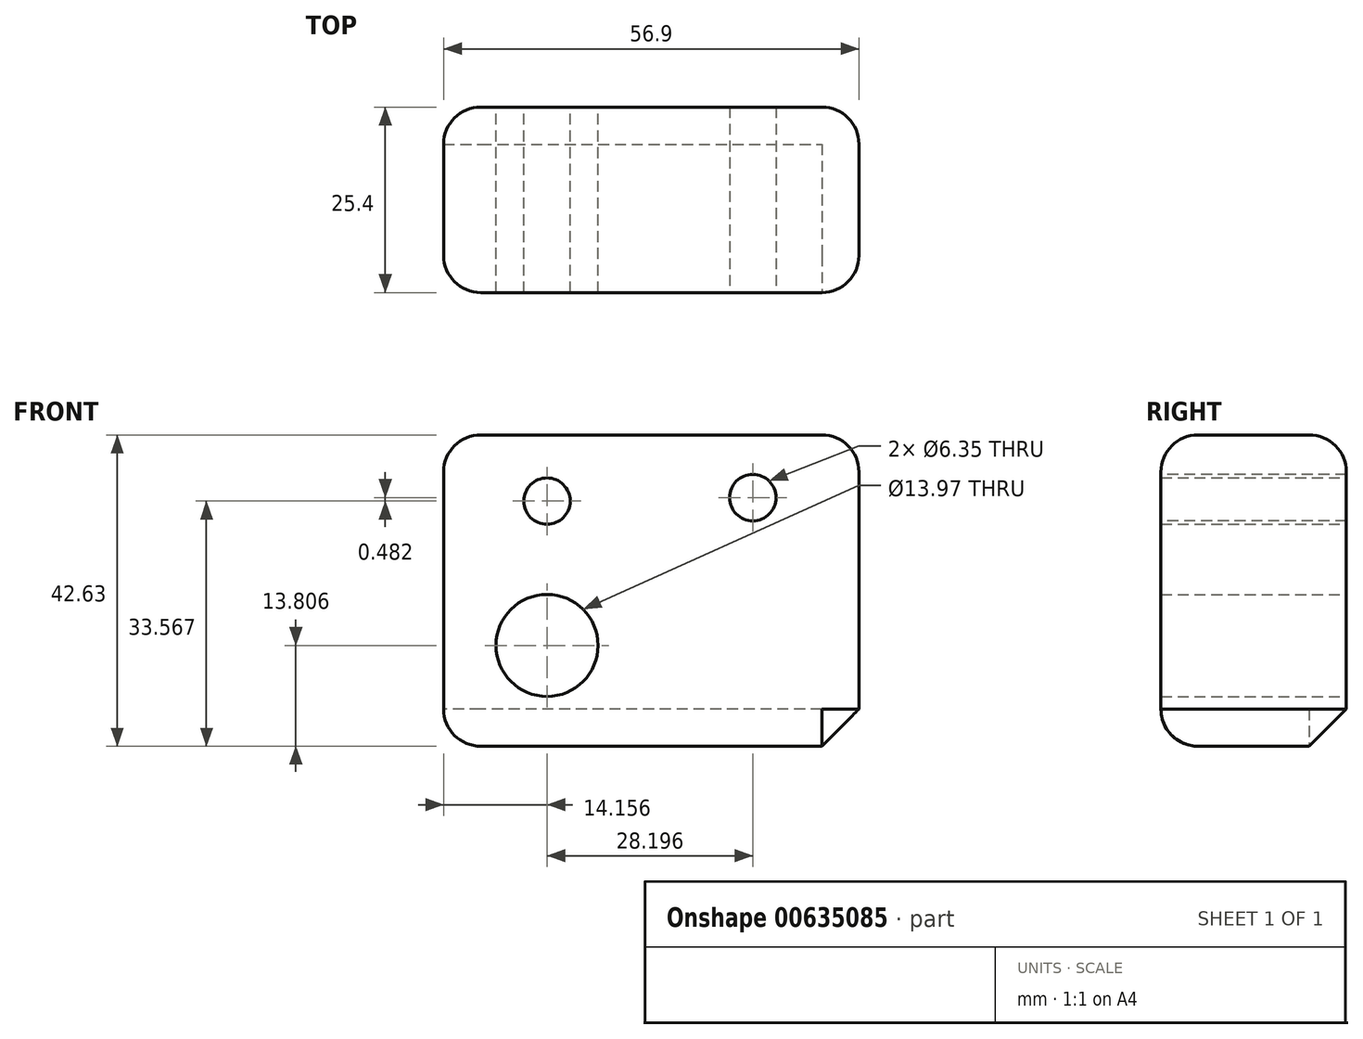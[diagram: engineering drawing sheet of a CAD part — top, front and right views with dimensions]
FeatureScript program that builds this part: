
annotation { "Feature Type Name" : "Feature", "Feature Type Description" : "" }
export const myFeature = defineFeature(function(context is Context, id is Id, definition is map)
    precondition{}
    {
        {
            var Q0;
            Q0=qCreatedBy(makeId("Front.planeOp"),FACE);
            var sketch = newSketch(context, id + "F0", { "sketchPlane" : qUnion([Q0])});
            skLineSegment(sketch, "E0.bottom", {"start": v(-32.11, 18.1) * mm, "end": v(24.79, 18.1) * mm});
            skLineSegment(sketch, "E0.top", {"start": v(-32.11, -24.53) * mm, "end": v(24.79, -24.53) * mm});
            skLineSegment(sketch, "E0.left", {"start": v(-32.11, 18.1) * mm, "end": v(-32.11, -24.53) * mm});
            skLineSegment(sketch, "E0.right", {"start": v(24.79, 18.1) * mm, "end": v(24.79, -24.53) * mm});
            skSolve(sketch);
        }
        {
            var Q0;
            Q0=makeQuery(id+"F0.imprint","IMPRINT",FACE,{"disambiguationData":[TD([[makeQuery(id+"F0.imprint","IMPRINT",EDGE,{"derivedFrom":sQuery(id+"F0.wireOp",EDGE,"E0.bottom")}),-1.0]])]});
            extrude(context, id + "F1", {"entities" : qUnion([Q0]), "oppositeDirection" : true, "depth" : 25.4 * mm, "offsetDistance" : 25.4 * mm});
        }
        {
            var Q0;
            Q0=qCreatedBy(makeId("Front.planeOp"),FACE);
            var sketch = newSketch(context, id + "F2", { "sketchPlane" : qUnion([Q0])});
            skCircle(sketch, "E1", {"center": v(10.24, 9.52) * mm, "radius": 5.03 * mm});
            skCircle(sketch, "E2", {"center": v(-5.18, 9.28) * mm, "radius": 2.06 * mm});
            skSolve(sketch);
        }
        {
            var Q0;
            Q0=sQuery(id+"F2.wireOp",VERTEX,"E1.center");
            var Q1;
            Q1=makeQuery(id+"F1.opExtrude","SWEPT_BODY",BODY,{"disambiguationData":[OSD([sQuery(id+"F0.wireOp",EDGE,"E0.bottom"),sQuery(id+"F0.wireOp",EDGE,"E0.top"),sQuery(id+"F0.wireOp",EDGE,"E0.left"),sQuery(id+"F0.wireOp",EDGE,"E0.right")])]});
            hole(context, id + "F3", {"style" : HoleStyle.SIMPLE, "endStyle" : HoleEndStyle.THROUGH, "holeDiameter" : 6.35 * mm, "majorDiameter" : 6.35 * mm, "isTappedThrough" : true, "tappedDepth" : 12.7 * mm, "tapClearance" : 3, "locations" : qUnion([Q0]), "scope" : qUnion([Q1])});
        }
        {
            var Q0;
            Q0=makeQuery(id+"F1.opExtrude","CAP_FACE",FACE,{"disambiguationData":[OSD([sQuery(id+"F0.wireOp",EDGE,"E0.bottom"),sQuery(id+"F0.wireOp",EDGE,"E0.top"),sQuery(id+"F0.wireOp",EDGE,"E0.left"),sQuery(id+"F0.wireOp",EDGE,"E0.right")])],"isStart":false});
            var sketch = newSketch(context, id + "F4", { "sketchPlane" : qUnion([Q0])});
            skCircle(sketch, "E3", {"center": v(17.95, 9.04) * mm, "radius": 3.58 * mm});
            skSolve(sketch);
        }
        {
            var Q0;
            Q0=sQuery(id+"F4.wireOp",VERTEX,"E3.center");
            var Q1;
            Q1=makeQuery(id+"F1.opExtrude","SWEPT_BODY",BODY,{"disambiguationData":[OSD([sQuery(id+"F0.wireOp",EDGE,"E0.bottom"),sQuery(id+"F0.wireOp",EDGE,"E0.top"),sQuery(id+"F0.wireOp",EDGE,"E0.left"),sQuery(id+"F0.wireOp",EDGE,"E0.right")])]});
            hole(context, id + "F5", {"style" : HoleStyle.SIMPLE, "endStyle" : HoleEndStyle.THROUGH, "holeDiameter" : 6.35 * mm, "majorDiameter" : 6.35 * mm, "isTappedThrough" : true, "tappedDepth" : 12.7 * mm, "tapClearance" : 3, "locations" : qUnion([Q0]), "scope" : qUnion([Q1])});
        }
        {
            var Q0;
            Q0=makeQuery(id+"F1.opExtrude","CAP_FACE",FACE,{"disambiguationData":[OSD([sQuery(id+"F0.wireOp",EDGE,"E0.bottom"),sQuery(id+"F0.wireOp",EDGE,"E0.top"),sQuery(id+"F0.wireOp",EDGE,"E0.left"),sQuery(id+"F0.wireOp",EDGE,"E0.right")])],"isStart":false});
            var sketch = newSketch(context, id + "F6", { "sketchPlane" : qUnion([Q0])});
            skSolve(sketch);
        }
        {
            var Q0;
            {var subQ3=sQuery(id+"F0.wireOp",EDGE,"E0.bottom");Q0=makeQuery(id+"F6.imprint","IMPRINT",FACE,{"disambiguationData":[TD([[makeQuery(id+"F6.imprint","IMPRINT",EDGE,{"derivedFrom":makeQuery(id+"F1.opExtrude","CAP_EDGE",EDGE,{"disambiguationData":[OSD([subQ3])],"isStart":false})}),1.0]])]});}
            var sketch = newSketch(context, id + "F7", { "sketchPlane" : qUnion([Q0])});
            skCircle(sketch, "E4", {"center": v(17.95, -10.72) * mm, "radius": 9 * mm});
            skSolve(sketch);
        }
        {
            var Q0;
            Q0=sQuery(id+"F7.wireOp",VERTEX,"E4.center");
            var Q1;
            Q1=makeQuery(id+"F1.opExtrude","SWEPT_BODY",BODY,{"disambiguationData":[OSD([sQuery(id+"F0.wireOp",EDGE,"E0.bottom"),sQuery(id+"F0.wireOp",EDGE,"E0.top"),sQuery(id+"F0.wireOp",EDGE,"E0.left"),sQuery(id+"F0.wireOp",EDGE,"E0.right")])]});
            hole(context, id + "F8", {"style" : HoleStyle.SIMPLE, "endStyle" : HoleEndStyle.THROUGH, "holeDiameter" : 13.97 * mm, "majorDiameter" : 6.35 * mm, "isTappedThrough" : true, "tappedDepth" : 12.7 * mm, "tapClearance" : 3, "locations" : qUnion([Q0]), "scope" : qUnion([Q1])});
        }
        {
            var Q0;
            Q0=makeQuery(id+"F1.opExtrude","CAP_EDGE",EDGE,{"disambiguationData":[OSD([sQuery(id+"F0.wireOp",EDGE,"E0.left")])],"isStart":true});
            var Q1;
            Q1=makeQuery(id+"F1.opExtrude","CAP_EDGE",EDGE,{"disambiguationData":[OSD([sQuery(id+"F0.wireOp",EDGE,"E0.left")])],"isStart":false});
            var Q2;
            Q2=makeQuery(id+"F1.opExtrude","SWEPT_EDGE",EDGE,{"disambiguationData":[OSD([sQuery(id+"F0.wireOp",EDGE,"E0.bottom"),sQuery(id+"F0.wireOp",EDGE,"E0.left")])]});
            var Q3;
            Q3=makeQuery(id+"F1.opExtrude","SWEPT_EDGE",EDGE,{"disambiguationData":[OSD([sQuery(id+"F0.wireOp",EDGE,"E0.top"),sQuery(id+"F0.wireOp",EDGE,"E0.left")])]});
            var Q4;
            Q4=makeQuery(id+"F1.opExtrude","CAP_EDGE",EDGE,{"disambiguationData":[OSD([sQuery(id+"F0.wireOp",EDGE,"E0.top")])],"isStart":true});
            var Q5;
            Q5=makeQuery(id+"F1.opExtrude","CAP_EDGE",EDGE,{"disambiguationData":[OSD([sQuery(id+"F0.wireOp",EDGE,"E0.bottom")])],"isStart":true});
            var Q6;
            Q6=makeQuery(id+"F1.opExtrude","CAP_EDGE",EDGE,{"disambiguationData":[OSD([sQuery(id+"F0.wireOp",EDGE,"E0.right")])],"isStart":true});
            var Q7;
            Q7=makeQuery(id+"F1.opExtrude","CAP_EDGE",EDGE,{"disambiguationData":[OSD([sQuery(id+"F0.wireOp",EDGE,"E0.bottom")])],"isStart":false});
            var Q8;
            Q8=makeQuery(id+"F1.opExtrude","CAP_EDGE",EDGE,{"disambiguationData":[OSD([sQuery(id+"F0.wireOp",EDGE,"E0.right")])],"isStart":false});
            var Q9;
            Q9=makeQuery(id+"F1.opExtrude","SWEPT_EDGE",EDGE,{"disambiguationData":[OSD([sQuery(id+"F0.wireOp",EDGE,"E0.bottom"),sQuery(id+"F0.wireOp",EDGE,"E0.right")])]});
            fillet(context, id + "F9", {"entities" : qUnion([Q0, Q1, Q2, Q3, Q4, Q5, Q6, Q7, Q8, Q9]), "radius" : 5.08 * mm, "tangentPropagation" : true, "allowEdgeOverflow" : false});
        }
        {
            var Q0;
            Q0=makeQuery(id+"F1.opExtrude","CAP_EDGE",EDGE,{"disambiguationData":[OSD([sQuery(id+"F0.wireOp",EDGE,"E0.top")])],"isStart":false});
            chamfer(context, id + "F10", {"entities" : qUnion([Q0]), "width" : 5.08 * mm, "tangentPropagation" : true});
        }
    });
